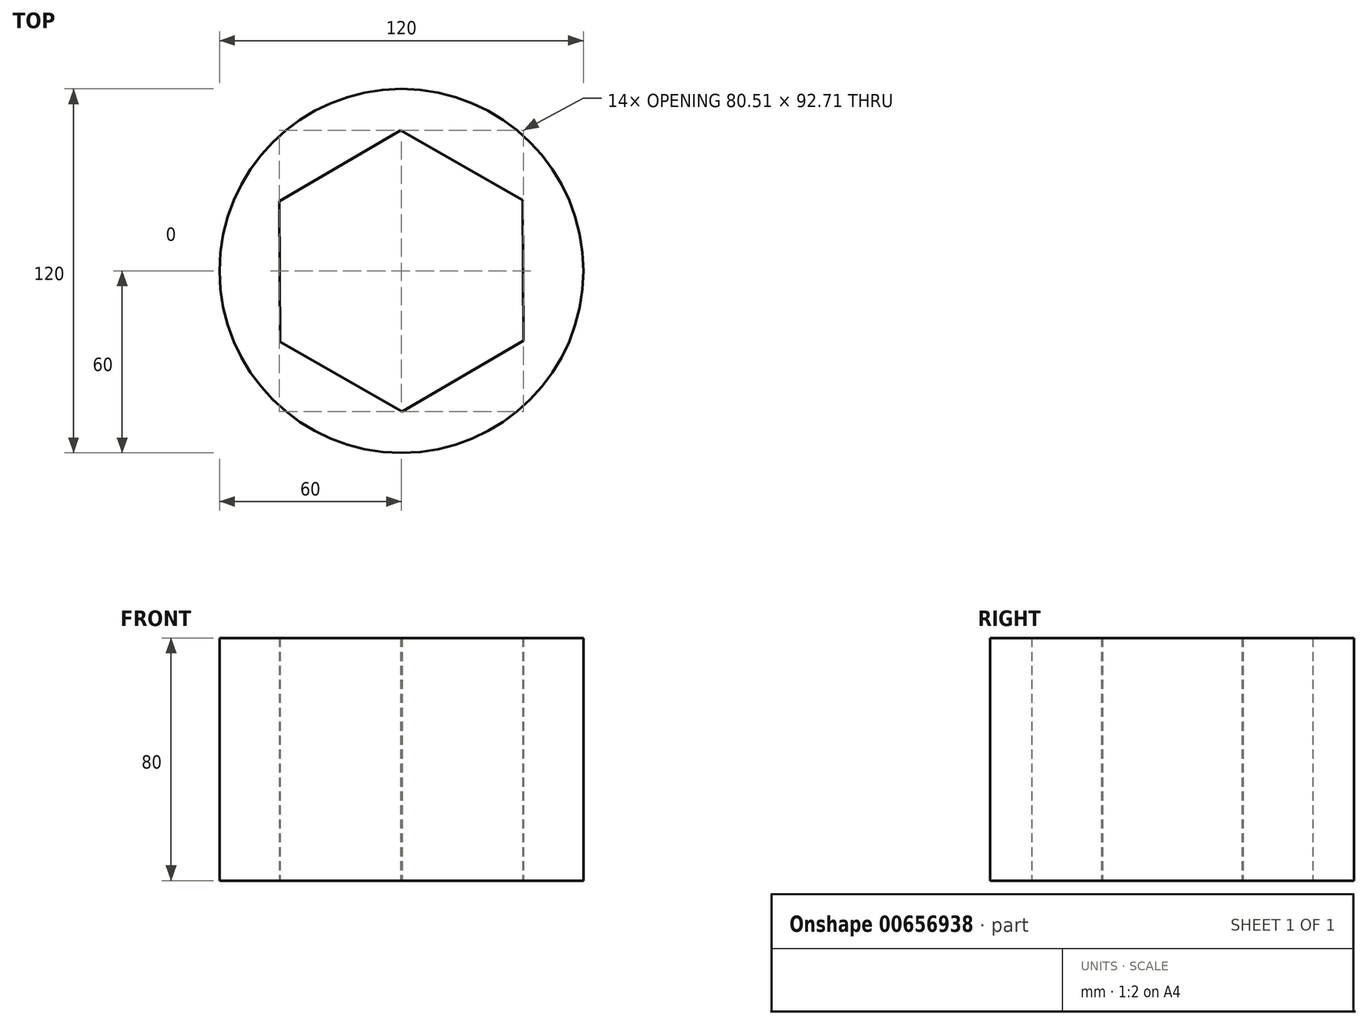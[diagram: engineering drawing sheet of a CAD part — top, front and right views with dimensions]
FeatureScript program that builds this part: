
annotation { "Feature Type Name" : "Feature", "Feature Type Description" : "" }
export const myFeature = defineFeature(function(context is Context, id is Id, definition is map)
    precondition{}
    {
        {
            var Q0;
            Q0=qCreatedBy(makeId("Top.planeOp"),FACE);
            var sketch = newSketch(context, id + "F0", { "sketchPlane" : qUnion([Q0])});
            skCircle(sketch, "E0", {"center": v(0, 0) * mm, "radius": 60 * mm});
            skCircle(sketch, "E1.cCircle", {"center": v(0, 0) * mm, "radius": 40.14 * mm, "construction": true});
            skLineSegment(sketch, "E1.0", {"start": v(-0.22, 46.35) * mm, "end": v(40.03, 23.37) * mm});
            skLineSegment(sketch, "E1.1", {"start": v(40.03, 23.37) * mm, "end": v(40.25, -22.99) * mm});
            skLineSegment(sketch, "E1.2", {"start": v(40.25, -22.99) * mm, "end": v(0.22, -46.35) * mm});
            skLineSegment(sketch, "E1.3", {"start": v(0.22, -46.35) * mm, "end": v(-40.03, -23.37) * mm});
            skLineSegment(sketch, "E1.4", {"start": v(-40.03, -23.37) * mm, "end": v(-40.25, 22.99) * mm});
            skLineSegment(sketch, "E1.5", {"start": v(-40.25, 22.99) * mm, "end": v(-0.22, 46.35) * mm});
            skPoint(sketch, "E1.0.midPoint", {"position": v(19.9, 34.86) * mm});
            skSolve(sketch);
        }
        {
            var Q0;
            Q0 = qSketchRegion(id + "F0", true);
            extrude(context, id + "F1", {"entities" : qUnion([Q0]), "depth" : 80 * mm, "offsetDistance" : 25 * mm});
        }
    });
